# Revit family: Napkin_Disposal-Bobrick-TrimLineSeries-B-35303
name_source: partatom
category: Specialty Equipment
revit_build: Autodesk Revit 2014 (Build: 20130308_1515(x64)
units: mm (PartAtom-declared; Revit-internal decimal feet)

## types (1)
- B-35303
    Assembly Code = C1030200
    Default Elevation = 30"
    Description = TrimLineSeries Recessed Sanitary Napkin Disposal
    Height = 18 15/16"
    Installation Type = Recessed in Wall
    Length = 9/16"
    Manufacturer = Bobrick
    Material = Stainless Steel-Bobrick-Typre 304-Satin
    Model = B-35303
    Price = Prices may vary. Please consult Manufacturer Representative for most up-to-date price list.
    Product Documentation Link = http://products.bobrick.com
    Product Page URL = http://products.bobrick.com
    Revised Date = 02/07/2019
    URL = http://www.bobrick.com
    Warranty Documentation Link = http://products.bobrick.com
    Width = 13"

## geometry (parser evidence)
native form markers: Sweep x3
no freeform markers — native parametric forms only
